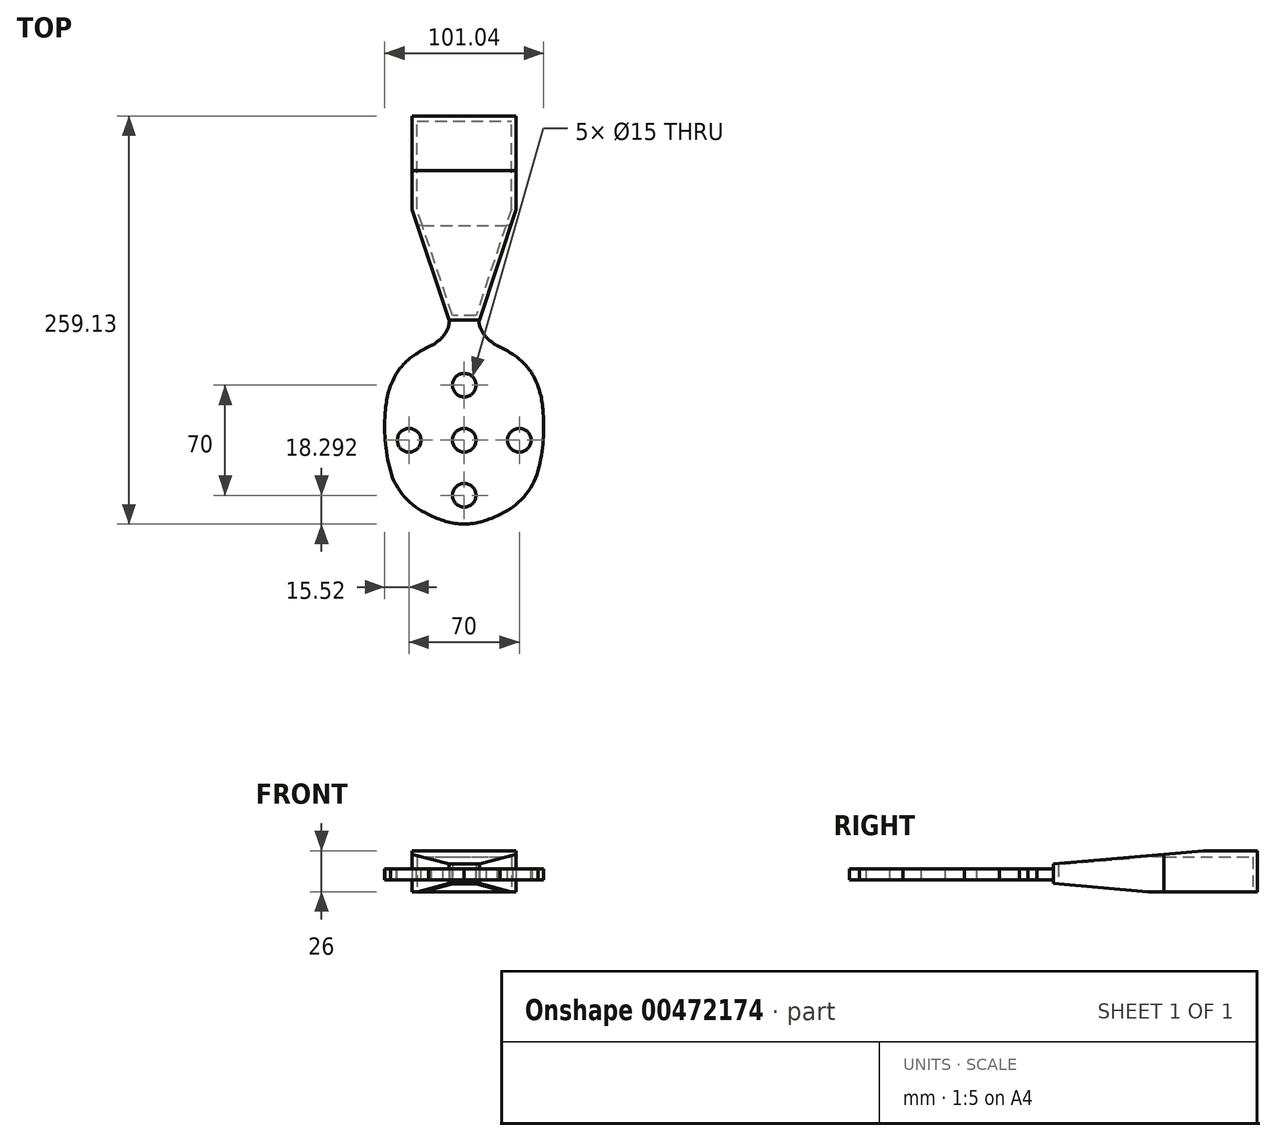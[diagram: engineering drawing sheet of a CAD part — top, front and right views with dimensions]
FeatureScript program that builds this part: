
annotation { "Feature Type Name" : "Feature", "Feature Type Description" : "" }
export const myFeature = defineFeature(function(context is Context, id is Id, definition is map)
    precondition{}
    {
        {
            var Q0;
            Q0=qCreatedBy(makeId("Top.planeOp"),FACE);
            var sketch = newSketch(context, id + "F0", { "sketchPlane" : qUnion([Q0])});
            skArc(sketch, "E0", {"start": v(-13.73, 5.74) * mm, "mid": v(-10.56, 10.64) * mm, "end": v(-9.36, 16.34) * mm});
            skArc(sketch, "E1", {"start": v(-20.95, 0) * mm, "mid": v(-17.1, 2.58) * mm, "end": v(-13.73, 5.74) * mm});
            skArc(sketch, "E2", {"start": v(-20.95, 0) * mm, "mid": v(-25.93, -2.4) * mm, "end": v(-30.6, -5.37) * mm});
            skArc(sketch, "E3", {"start": v(-30.6, -5.37) * mm, "mid": v(-37.67, -10.93) * mm, "end": v(-43.2, -18.02) * mm});
            skArc(sketch, "E4", {"start": v(-43.2, -18.02) * mm, "mid": v(-47.88, -28.8) * mm, "end": v(-49.9, -40.39) * mm});
            skArc(sketch, "E5", {"start": v(-49.9, -40.39) * mm, "mid": v(-50.2, -60) * mm, "end": v(-46.92, -79.35) * mm});
            skArc(sketch, "E6", {"start": v(-46.92, -79.35) * mm, "mid": v(-37.9, -95.94) * mm, "end": v(-22.66, -107.07) * mm});
            skArc(sketch, "E7", {"start": v(-22.66, -107.07) * mm, "mid": v(-11.7, -111.54) * mm, "end": v(0, -113.3) * mm});
            skLineSegment(sketch, "E8", {"start": v(0, 107.82) * mm, "end": v(0, -228) * mm, "construction": true});
            skArc(sketch, "E9.MirrorCS", {"start": v(20.95, 0) * mm, "mid": v(17.1, 2.58) * mm, "end": v(13.73, 5.74) * mm});
            skArc(sketch, "E10.MirrorCS", {"start": v(13.73, 5.74) * mm, "mid": v(10.56, 10.64) * mm, "end": v(9.36, 16.34) * mm});
            skArc(sketch, "E11.MirrorCS", {"start": v(43.2, -18.02) * mm, "mid": v(47.88, -28.8) * mm, "end": v(49.9, -40.39) * mm});
            skArc(sketch, "E12.MirrorCS", {"start": v(49.9, -40.39) * mm, "mid": v(50.2, -60) * mm, "end": v(46.92, -79.35) * mm});
            skArc(sketch, "E13.MirrorCS", {"start": v(30.6, -5.37) * mm, "mid": v(37.67, -10.93) * mm, "end": v(43.2, -18.02) * mm});
            skArc(sketch, "E14.MirrorCS", {"start": v(20.95, 0) * mm, "mid": v(25.93, -2.4) * mm, "end": v(30.6, -5.37) * mm});
            skArc(sketch, "E15.MirrorCS", {"start": v(46.92, -79.35) * mm, "mid": v(37.9, -95.94) * mm, "end": v(22.66, -107.07) * mm});
            skArc(sketch, "E16.MirrorCS", {"start": v(22.66, -107.07) * mm, "mid": v(11.7, -111.54) * mm, "end": v(0, -113.3) * mm});
            skLineSegment(sketch, "E17", {"start": v(-9.36, 16.34) * mm, "end": v(9.36, 16.34) * mm});
            skSolve(sketch);
        }
        {
            var Q0;
            Q0 = qSketchRegion(id + "F0", true);
            extrude(context, id + "F1", {"entities" : qUnion([Q0]), "endBound" : BoundingType.SYMMETRIC, "depth" : 7 * mm});
        }
        {
            var Q0;
            Q0=qCreatedBy(makeId("Top.planeOp"),FACE);
            var sketch = newSketch(context, id + "F2", { "sketchPlane" : qUnion([Q0])});
            skLineSegment(sketch, "E18", {"start": v(-7.5, 19.34) * mm, "end": v(-30, 86.83) * mm});
            skLineSegment(sketch, "E19", {"start": v(30, 86.83) * mm, "end": v(7.5, 19.34) * mm});
            skLineSegment(sketch, "E20", {"start": v(7.5, 19.34) * mm, "end": v(-7.5, 19.34) * mm});
            skPoint(sketch, "E21", {"position": v(0, 19.34) * mm});
            skLineSegment(sketch, "E22.0", {"start": v(9.66, 16.34) * mm, "end": v(-9.66, 16.34) * mm});
            skLineSegment(sketch, "E22.1", {"start": v(33, 86.34) * mm, "end": v(9.66, 16.34) * mm});
            skLineSegment(sketch, "E22.3", {"start": v(-9.66, 16.34) * mm, "end": v(-33, 86.34) * mm});
            skLineSegment(sketch, "E23", {"start": v(-33, 86.34) * mm, "end": v(-33, 145.83) * mm});
            skLineSegment(sketch, "E24", {"start": v(-30, 86.83) * mm, "end": v(-30, 142.83) * mm});
            skLineSegment(sketch, "E25", {"start": v(30, 86.83) * mm, "end": v(30, 142.83) * mm});
            skLineSegment(sketch, "E26", {"start": v(33, 86.34) * mm, "end": v(33, 145.83) * mm});
            skLineSegment(sketch, "E27", {"start": v(-30, 142.83) * mm, "end": v(30, 142.83) * mm});
            skLineSegment(sketch, "E28", {"start": v(-33, 145.83) * mm, "end": v(33, 145.83) * mm});
            skPoint(sketch, "E29", {"position": v(0, 145.83) * mm});
            skSolve(sketch);
        }
        {
            var Q0;
            Q0 = qSketchRegion(id + "F2", true);
            extrude(context, id + "F3", {"entities" : qUnion([Q0]), "endBound" : BoundingType.SYMMETRIC, "depth" : 22 * mm});
        }
        {
            var Q0;
            Q0=makeQuery(id+"F3.opExtrude","CAP_EDGE",EDGE,{"disambiguationData":[OSD([sQuery(id+"F2.wireOp",EDGE,"E22.0")])],"isStart":true});
            var Q1;
            Q1=makeQuery(id+"F3.opExtrude","CAP_EDGE",EDGE,{"disambiguationData":[OSD([sQuery(id+"F2.wireOp",EDGE,"E22.0")])],"isStart":false});
            chamfer(context, id + "F4", {"entities" : qUnion([Q0, Q1]), "chamferType" : ChamferType.OFFSET_ANGLE, "width" : 60 * mm, "oppositeDirection" : false, "angle" : 5 * degree, "tangentPropagation" : true});
        }
        {
            var Q0;
            Q0=makeQuery(id+"F3.opExtrude","CAP_FACE",FACE,{"disambiguationData":[OSD([sQuery(id+"F2.wireOp",EDGE,"E18"),sQuery(id+"F2.wireOp",EDGE,"E19"),sQuery(id+"F2.wireOp",EDGE,"E20"),sQuery(id+"F2.wireOp",EDGE,"E22.0"),sQuery(id+"F2.wireOp",EDGE,"E22.1"),sQuery(id+"F2.wireOp",EDGE,"E22.3"),sQuery(id+"F2.wireOp",EDGE,"E23"),sQuery(id+"F2.wireOp",EDGE,"E24"),sQuery(id+"F2.wireOp",EDGE,"E25"),sQuery(id+"F2.wireOp",EDGE,"E26"),sQuery(id+"F2.wireOp",EDGE,"E27"),sQuery(id+"F2.wireOp",EDGE,"E28")])],"isStart":false});
            var sketch = newSketch(context, id + "F5", { "sketchPlane" : qUnion([Q0])});
            skLineSegment(sketch, "E30.0.0", {"start": v(-33, 86.34) * mm, "end": v(-29.67, 76.34) * mm});
            skLineSegment(sketch, "E30.0.8", {"start": v(29.67, 76.34) * mm, "end": v(33, 86.34) * mm});
            skLineSegment(sketch, "E30.0.9", {"start": v(33, 86.34) * mm, "end": v(33, 145.83) * mm});
            skLineSegment(sketch, "E30.0.10", {"start": v(33, 145.83) * mm, "end": v(-33, 145.83) * mm});
            skLineSegment(sketch, "E30.0.11", {"start": v(-33, 145.83) * mm, "end": v(-33, 86.34) * mm});
            skLineSegment(sketch, "E31", {"start": v(-29.67, 76.34) * mm, "end": v(29.67, 76.34) * mm});
            skSolve(sketch);
        }
        {
            var Q0;
            Q0 = qSketchRegion(id + "F5", true);
            extrude(context, id + "F6", {"entities" : qUnion([Q0]), "depth" : 4 * mm});
        }
        {
            var Q0;
            Q0=makeQuery(id+"F6.opExtrude","CAP_FACE",FACE,{"disambiguationData":[OSD([sQuery(id+"F5.wireOp",EDGE,"E30.0.0"),sQuery(id+"F5.wireOp",EDGE,"E30.0.8"),sQuery(id+"F5.wireOp",EDGE,"E30.0.9"),sQuery(id+"F5.wireOp",EDGE,"E30.0.10"),sQuery(id+"F5.wireOp",EDGE,"E30.0.11"),sQuery(id+"F5.wireOp",EDGE,"E31")])],"isStart":false});
            var sketch = newSketch(context, id + "F7", { "sketchPlane" : qUnion([Q0])});
            skLineSegment(sketch, "E32.0.2", {"start": v(-9.66, 16.34) * mm, "end": v(-29.67, 76.34) * mm});
            skLineSegment(sketch, "E32.0.3", {"start": v(-9.66, 16.34) * mm, "end": v(9.66, 16.34) * mm});
            skLineSegment(sketch, "E32.0.4", {"start": v(29.67, 76.34) * mm, "end": v(9.66, 16.34) * mm});
            skLineSegment(sketch, "E33", {"start": v(-29.67, 76.34) * mm, "end": v(29.67, 76.34) * mm});
            skSolve(sketch);
        }
        {
            var Q0;
            Q0 = qSketchRegion(id + "F7", true);
            var Q1;
            {var subQ0=sQuery(id+"F2.wireOp",EDGE,"E22.0");Q1=makeQuery(id+"F4.opChamfer","BLEND_FACE",FACE,{"disambiguationData":[OSD([subQ0]),TDD([makeQuery(id+"F3.opExtrude","CAP_EDGE",EDGE,{"disambiguationData":[OSD([subQ0])],"isStart":false})])]});}
            extrude(context, id + "F8", {"entities" : qUnion([Q0]), "operationType" : NewBodyOperationType.ADD, "endBound" : BoundingType.UP_TO_SURFACE, "oppositeDirection" : true, "endBoundEntityFace" : qUnion([Q1]), "depth" : 25 * mm});
        }
        {
            var Q0;
            Q0=makeQuery(id+"F8.opExtrude","CAP_EDGE",EDGE,{"disambiguationData":[OSD([sQuery(id+"F7.wireOp",EDGE,"E32.0.3")])],"isStart":true});
            chamfer(context, id + "F9", {"entities" : qUnion([Q0]), "chamferType" : ChamferType.OFFSET_ANGLE, "width" : 95 * mm, "oppositeDirection" : false, "angle" : 5 * degree, "tangentPropagation" : true});
        }
        {
            var Q0;
            Q0=makeQuery(id+"F1.opExtrude","CAP_FACE",FACE,{"disambiguationData":[OSD([sQuery(id+"F0.wireOp",EDGE,"E0"),sQuery(id+"F0.wireOp",EDGE,"E1"),sQuery(id+"F0.wireOp",EDGE,"E2"),sQuery(id+"F0.wireOp",EDGE,"E3"),sQuery(id+"F0.wireOp",EDGE,"E4"),sQuery(id+"F0.wireOp",EDGE,"E5"),sQuery(id+"F0.wireOp",EDGE,"E6"),sQuery(id+"F0.wireOp",EDGE,"E7"),sQuery(id+"F0.wireOp",EDGE,"E9.MirrorCS"),sQuery(id+"F0.wireOp",EDGE,"E10.MirrorCS"),sQuery(id+"F0.wireOp",EDGE,"E11.MirrorCS"),sQuery(id+"F0.wireOp",EDGE,"E12.MirrorCS"),sQuery(id+"F0.wireOp",EDGE,"E13.MirrorCS"),sQuery(id+"F0.wireOp",EDGE,"E14.MirrorCS"),sQuery(id+"F0.wireOp",EDGE,"E15.MirrorCS"),sQuery(id+"F0.wireOp",EDGE,"E16.MirrorCS"),sQuery(id+"F0.wireOp",EDGE,"E17")])],"isStart":false});
            var sketch = newSketch(context, id + "F10", { "sketchPlane" : qUnion([Q0])});
            skLineSegment(sketch, "E34", {"start": v(-50.2, -60) * mm, "end": v(50.2, -60) * mm, "construction": true});
            skCircle(sketch, "E35", {"center": v(0, -60) * mm, "radius": 35 * mm, "construction": true});
            skCircle(sketch, "E36", {"center": v(0, -25) * mm, "radius": 7.5 * mm});
            skCircle(sketch, "E37.1.0", {"center": v(-35, -60) * mm, "radius": 7.5 * mm});
            skCircle(sketch, "E37.2.0", {"center": v(0, -95) * mm, "radius": 7.5 * mm});
            skCircle(sketch, "E37.3.0", {"center": v(35, -60) * mm, "radius": 7.5 * mm});
            skCircle(sketch, "E38", {"center": v(0, -60) * mm, "radius": 7.5 * mm});
            skSolve(sketch);
        }
        {
            var Q0;
            Q0 = qSketchRegion(id + "F10", true);
            extrude(context, id + "F11", {"entities" : qUnion([Q0]), "operationType" : NewBodyOperationType.REMOVE, "oppositeDirection" : true, "depth" : 25 * mm});
        }
    });
